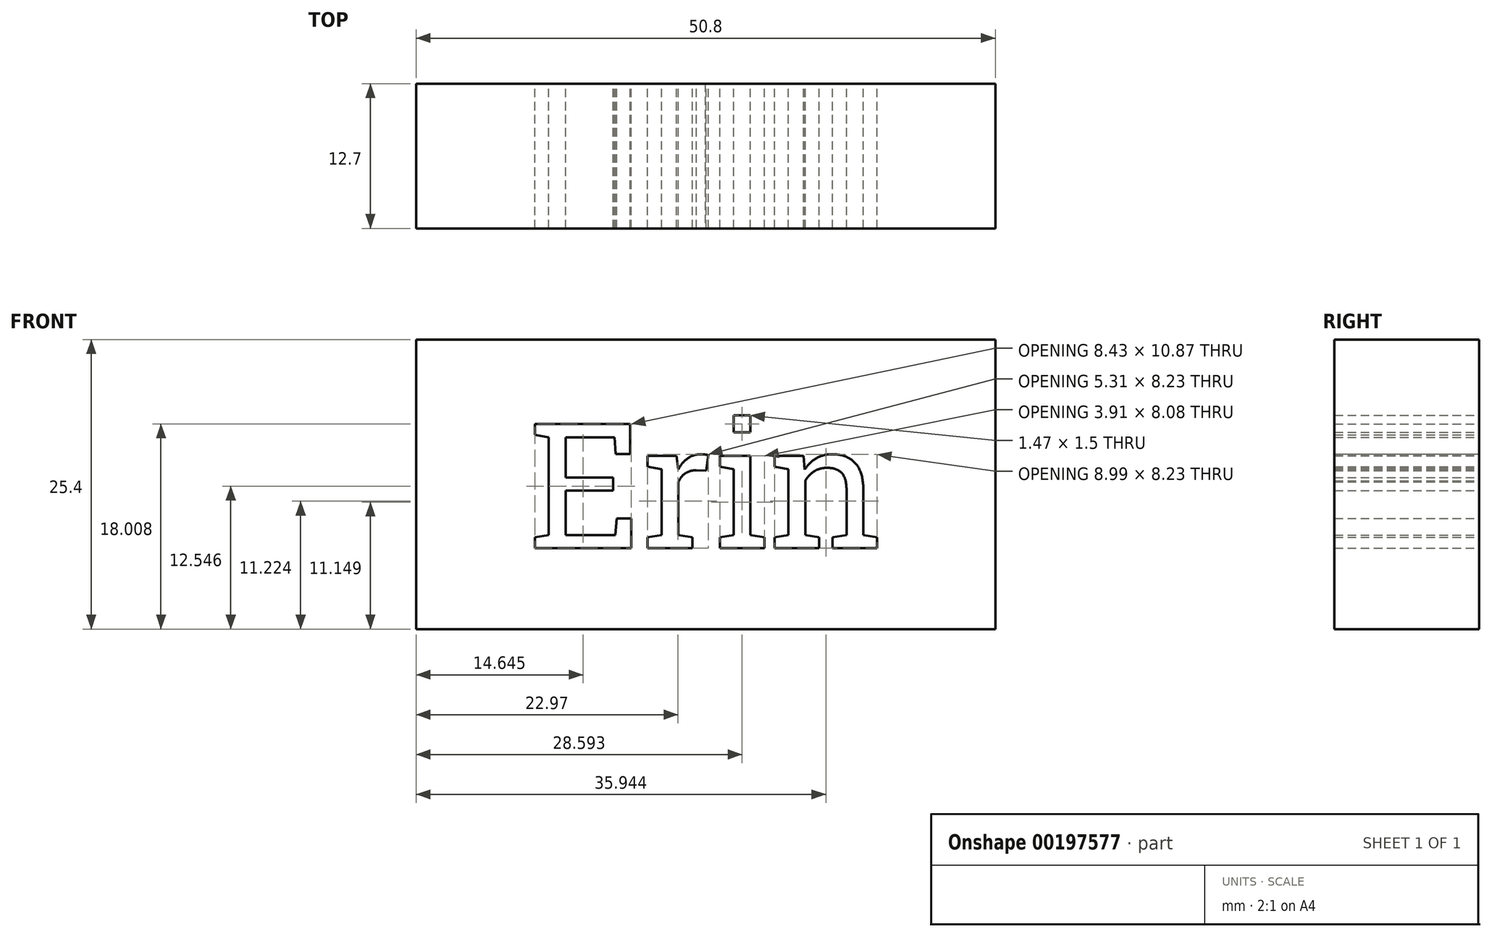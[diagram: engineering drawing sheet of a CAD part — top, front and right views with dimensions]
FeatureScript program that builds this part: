
annotation { "Feature Type Name" : "Feature", "Feature Type Description" : "" }
export const myFeature = defineFeature(function(context is Context, id is Id, definition is map)
    precondition{}
    {
        {
            var Q0;
            Q0=qCreatedBy(makeId("Front.planeOp"),FACE);
            var sketch = newSketch(context, id + "F0", { "sketchPlane" : qUnion([Q0])});
            skLineSegment(sketch, "E0.bottom", {"start": v(-25.4, 12.7) * mm, "end": v(25.4, 12.7) * mm});
            skLineSegment(sketch, "E0.top", {"start": v(-25.4, -12.7) * mm, "end": v(25.4, -12.7) * mm});
            skLineSegment(sketch, "E0.left", {"start": v(-25.4, 12.7) * mm, "end": v(-25.4, -12.7) * mm});
            skLineSegment(sketch, "E0.right", {"start": v(25.4, 12.7) * mm, "end": v(25.4, -12.7) * mm});
            skPoint(sketch, "E0.middle", {"position": v(0, 0) * mm});
            skText(sketch, "E1", { "text": "Erin", "fontName": "RobotoSlab-Regular.ttf"});
            const initialGuessF0  = {"E1": [-0.0155, -0.00559, 1, 0, 0.01101]};
            skSetInitialGuess(sketch, initialGuessF0);
            skSolve(sketch);
        }
        {
            var Q0;
            Q0=makeQuery(id+"F0.imprint","IMPRINT",FACE,{"disambiguationData":[TD([[makeQuery(id+"F0.imprint","IMPRINT",EDGE,{"derivedFrom":sQuery(id+"F0.wireOp",EDGE,"E0.bottom")}),-1.0]])]});
            extrude(context, id + "F1", {"entities" : qUnion([Q0]), "depth" : 12.7 * mm});
        }
    });
